# Revit family: P300299-012
name_source: partatom
category: Lighting Fixtures
revit_build: Autodesk Revit 2014 (Build: 20130308_1515(x64)
units: mm (PartAtom-declared; Revit-internal decimal feet)

## types (1)
- P300299-012
    Apparent Load = 100 VA
    Assembly Code = D5020200
    Color Filter = 16777215
    Connector Description = Lighting Connector
    Default Elevation = 48 "
    Description = Clarion Collection One-Light Satin Brass and Clear Glass Modern Style Bath Vanity Wall Light
    Dimming Lamp Color Temperature Shift = <None>
    Features = Embrace minimalist simplicity with the Clarion Collection 1-Light Satin Brass Clear Glass Modern Bath Vanity Light. The square backplate and rounded light base are coated in a golden satin brass finish for a modern aesthetic. A light source glows from inside a cylindrical shade for a crisp, clean look.
Application: Embrace minimalist simplicity with the Clarion Collection 1-Light Satin Brass Clear Glass Modern Bath Vanity Light ideal for any entryway, hallway, foyer, bedroom, sitting room, or bathroom.
Styles: Perfect for contemporary, modern, and transitional style settings.
Finish: The square backplate and rounded light base are coated in a golden satin brass finish for a modern aesthetic.
Materials: Constructed from steel to ensure a long product lifespan. Mount the light fixture facing up or down.
Glass: A light source glows from inside a cylindrical shade for a crisp, clean look.
Bulbs: For ideal illumination, use 1 medium base T-lamp bulb that is sold separately (100w max - LED/CFL/incandescent). Compatible with dimmable bulbs.
Dimensions: Measures 5-inch width by 12-inch height by 4-1/4-inch extends.
Certifications: cULus damp location listed.
Pairs With: Pairs with Equinox, Cahill, and Bonita collections.
Warranty: Our 1-Year Limited Warranty guarantees your complete satisfaction with your purchase and includes professional after-sales customer service support.
    Fixture distribution = Direct
    Glass = Paint - Hubbell - White Texture
    Gold = Hubbell - Gold
    Housing Material = Paint - Hubbell - Metallic Brass
    Lamp = LED/CFL/incandescent
    Load Classification = Lighting
    Manufacturer = Progress Lighting
    Model = P300299-012
    Photometric Web File = generic
    Power Factor = 1
    Product Documentation Link = https://hubbellcdn.com
    Product Link = https://www.hubbell.com
    Tilt Angle = 60.00°
    URL = https://www.hubbell.com
    Voltage = 120 V
    Warranty = 1 year Warranty
    Wattage Comments = 100W
    Watts = 100 W

## geometry (parser evidence)
native form markers: Sweep x5
no freeform markers — native parametric forms only
